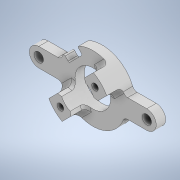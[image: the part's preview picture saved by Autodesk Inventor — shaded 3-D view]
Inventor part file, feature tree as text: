
AUTODESK INVENTOR PART (.ipt)
format: ipt  version: 2020 (Build 240168000, 168)  size: 313,344 bytes
history: native  units: mm
features: extrude x4, thicken_offset x4, sketch x4, fillet x3, projected_geometry x3, other x3, reference x2, chamfer x1
ambient origin geometry x8: Origin, YZ Plane, XZ Plane, XY Plane, X Axis, Y Axis, Z Axis, Center Point
bodies: Solid1 (feature_tree)
feature tree (24):
  extrude  "Extrusion1"  Depth=4.0mm
  extrude  "Extrusion2"  Depth=2.0mm TaperAngle=0.0deg
  thicken_offset  "Thicken1"
  chamfer  "Chamfer1"  Distance=5.207mm
  fillet  "Fillet1"  Radius=1.4mm
  fillet  "Fillet2"  Radius=1.4mm
  extrude  "Extrusion3"  Depth=2.0mm
  extrude  "Extrusion4"  Depth=2.0mm
  fillet  "Fillet3"  Radius=2.0mm
  thicken_offset  "Thicken2"
  thicken_offset  "Thicken3"
  thicken_offset  "Thicken4"
  sketch  "Sketch1"  dims[d0=4.0mm d1=7.8mm]
  reference  "Reference1"
  sketch  "Sketch2"  dims[d2=14.0mm d3=2.0mm d4=0.0mm]
  projected_geometry  "Projected Loop1"
  sketch  "Sketch3"  dims[d5=5.207mm]
  projected_geometry  "Projected Loop2"
  projected_geometry  "Projected Loop3"
  sketch  "Sketch4"  dims[d6=45.0deg d7=5.207mm d8=1.4mm d9=1.4mm d10=2.0mm d11=2.0mm d12=2.0mm d13=2.0mm d14=2.7mm d15=0.0mm d16=0.1mm d17=0.1mm d18=0.8mm d19=2.0mm d20=45.0deg d21=1.0mm d22=1.0mm d23=2.7mm d24=0.0mm d25=2.7mm d26=0.0mm d27=0.3mm d28=0.5mm d29=0.5mm d30=0.5mm d31=0.5mm d32=0.5mm d33=0.5mm]
  reference  "Reference2"
  parser-record x1  (decoder bookkeeping rows leaked as tree rows — omitted from the tree; the rows remain in map.json)
  other  "reducer_1.iam"
  other  "mot_holder_1:1"
note: 1 file-system path scrubbed to <path> (originals preserved in map.json)
